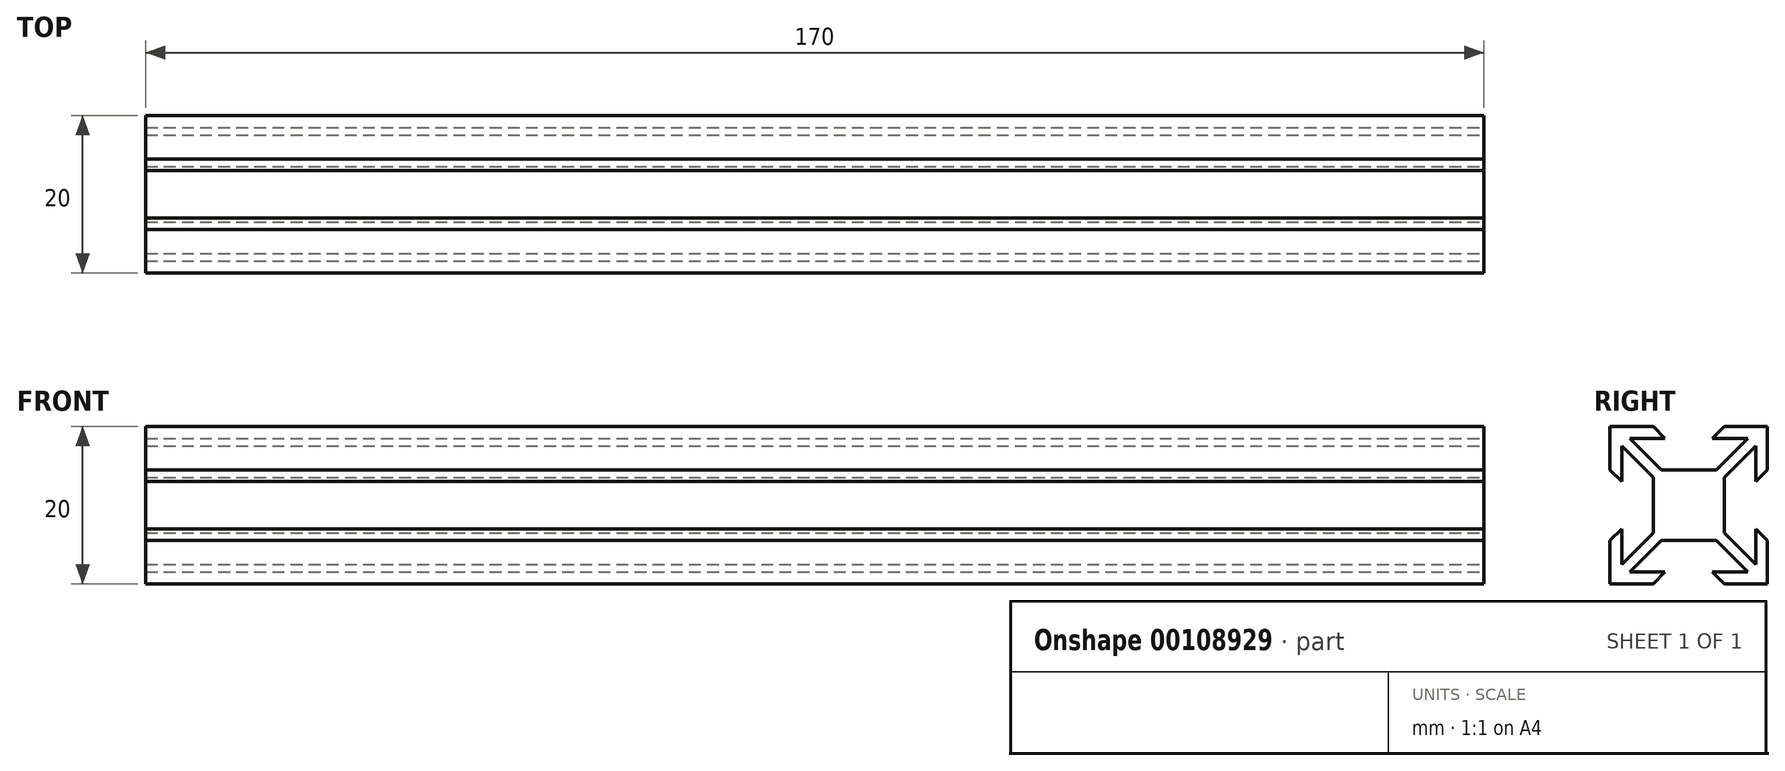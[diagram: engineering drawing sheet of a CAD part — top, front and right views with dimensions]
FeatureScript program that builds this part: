
annotation { "Feature Type Name" : "Feature", "Feature Type Description" : "" }
export const myFeature = defineFeature(function(context is Context, id is Id, definition is map)
    precondition{}
    {
        {
            var Q0;
            Q0=qCreatedBy(makeId("Top.planeOp"),FACE);
            var sketch = newSketch(context, id + "F0", { "sketchPlane" : qUnion([Q0])});
            skLineSegment(sketch, "E0.bottom", {"start": v(85, -10) * mm, "end": v(-85, -10) * mm});
            skLineSegment(sketch, "E0.top", {"start": v(85, 10) * mm, "end": v(-85, 10) * mm});
            skLineSegment(sketch, "E0.left", {"start": v(85, -10) * mm, "end": v(85, 10) * mm});
            skLineSegment(sketch, "E0.right", {"start": v(-85, -10) * mm, "end": v(-85, 10) * mm});
            skPoint(sketch, "E0.middle", {"position": v(0, 0) * mm});
            skSolve(sketch);
        }
        {
            var Q0;
            Q0 = qSketchRegion(id + "F0", true);
            extrude(context, id + "F1", {"entities" : qUnion([Q0]), "endBound" : BoundingType.SYMMETRIC, "depth" : 20 * mm});
        }
        {
            var Q0;
            Q0=makeQuery(id+"F1.opExtrude","SWEPT_FACE",FACE,{"disambiguationData":[OSD([sQuery(id+"F0.wireOp",EDGE,"E0.left")])]});
            var sketch = newSketch(context, id + "F2", { "sketchPlane" : qUnion([Q0])});
            skLineSegment(sketch, "E1", {"start": v(-4.5, 10) * mm, "end": v(-3, 8.5) * mm});
            skLineSegment(sketch, "E2", {"start": v(-3, 8.5) * mm, "end": v(-7.5, 8.5) * mm});
            skLineSegment(sketch, "E3", {"start": v(-7.5, 8.5) * mm, "end": v(-3.5, 4.5) * mm});
            skLineSegment(sketch, "E4", {"start": v(-3.5, 4.5) * mm, "end": v(0, 4.5) * mm});
            skLineSegment(sketch, "E5", {"start": v(-10, 4.5) * mm, "end": v(-8.5, 3) * mm});
            skLineSegment(sketch, "E6", {"start": v(-8.5, 3) * mm, "end": v(-8.5, 7.5) * mm});
            skLineSegment(sketch, "E7", {"start": v(-8.5, 7.5) * mm, "end": v(-4.5, 3.5) * mm});
            skLineSegment(sketch, "E8", {"start": v(-4.5, 3.5) * mm, "end": v(-4.5, 0) * mm});
            skLineSegment(sketch, "E9", {"start": v(-10, 0) * mm, "end": v(10, 0) * mm, "construction": true});
            skLineSegment(sketch, "E10", {"start": v(0, 10) * mm, "end": v(0, -10) * mm, "construction": true});
            skLineSegment(sketch, "E11.MirrorCS", {"start": v(4.5, 3.5) * mm, "end": v(4.5, 0) * mm});
            skLineSegment(sketch, "E12.MirrorCS", {"start": v(8.5, 7.5) * mm, "end": v(4.5, 3.5) * mm});
            skLineSegment(sketch, "E13.MirrorCS", {"start": v(8.5, 3) * mm, "end": v(8.5, 7.5) * mm});
            skLineSegment(sketch, "E14.MirrorCS", {"start": v(10, 4.5) * mm, "end": v(8.5, 3) * mm});
            skLineSegment(sketch, "E15.MirrorCS", {"start": v(3, 8.5) * mm, "end": v(7.5, 8.5) * mm});
            skLineSegment(sketch, "E16.MirrorCS", {"start": v(4.5, 10) * mm, "end": v(3, 8.5) * mm});
            skLineSegment(sketch, "E17.MirrorCS", {"start": v(7.5, 8.5) * mm, "end": v(3.5, 4.5) * mm});
            skLineSegment(sketch, "E18.MirrorCS", {"start": v(3.5, 4.5) * mm, "end": v(0, 4.5) * mm});
            skLineSegment(sketch, "E19.MirrorCS", {"start": v(-10, -4.5) * mm, "end": v(-8.5, -3) * mm});
            skLineSegment(sketch, "E20.MirrorCS", {"start": v(-8.5, -3) * mm, "end": v(-8.5, -7.5) * mm});
            skLineSegment(sketch, "E21.MirrorCS", {"start": v(-8.5, -7.5) * mm, "end": v(-4.5, -3.5) * mm});
            skLineSegment(sketch, "E22.MirrorCS", {"start": v(-7.5, -8.5) * mm, "end": v(-3.5, -4.5) * mm});
            skLineSegment(sketch, "E23.MirrorCS", {"start": v(-4.5, -10) * mm, "end": v(-3, -8.5) * mm});
            skLineSegment(sketch, "E24.MirrorCS", {"start": v(-4.5, -3.5) * mm, "end": v(-4.5, 0) * mm});
            skLineSegment(sketch, "E25.MirrorCS", {"start": v(-3.5, -4.5) * mm, "end": v(0, -4.5) * mm});
            skLineSegment(sketch, "E26.MirrorCS", {"start": v(-3, -8.5) * mm, "end": v(-7.5, -8.5) * mm});
            skLineSegment(sketch, "E27.MirrorCS", {"start": v(3.5, -4.5) * mm, "end": v(0, -4.5) * mm});
            skLineSegment(sketch, "E28.MirrorCS", {"start": v(7.5, -8.5) * mm, "end": v(3.5, -4.5) * mm});
            skLineSegment(sketch, "E29.MirrorCS", {"start": v(3, -8.5) * mm, "end": v(7.5, -8.5) * mm});
            skLineSegment(sketch, "E30.MirrorCS", {"start": v(4.5, -10) * mm, "end": v(3, -8.5) * mm});
            skLineSegment(sketch, "E31.MirrorCS", {"start": v(8.5, -7.5) * mm, "end": v(4.5, -3.5) * mm});
            skLineSegment(sketch, "E32.MirrorCS", {"start": v(8.5, -3) * mm, "end": v(8.5, -7.5) * mm});
            skLineSegment(sketch, "E33.MirrorCS", {"start": v(10, -4.5) * mm, "end": v(8.5, -3) * mm});
            skLineSegment(sketch, "E34.MirrorCS", {"start": v(4.5, -3.5) * mm, "end": v(4.5, 0) * mm});
            skSolve(sketch);
        }
        {
            var Q0;
            {var subQ0=sQuery(id+"F2.wireOp",EDGE,"E5");Q0=makeQuery(id+"F2.imprint","IMPRINT",FACE,{"disambiguationData":[TD([[makeQuery(id+"F2.imprint","IMPRINT",EDGE,{"derivedFrom":subQ0}),-1.0]])]});}
            var Q1;
            {var subQ0=sQuery(id+"F2.wireOp",EDGE,"E1");Q1=makeQuery(id+"F2.imprint","IMPRINT",FACE,{"disambiguationData":[TD([[makeQuery(id+"F2.imprint","IMPRINT",EDGE,{"derivedFrom":subQ0}),1.0]])]});}
            var Q2;
            Q2=makeQuery(id+"F2.imprint","IMPRINT",FACE,{"disambiguationData":[TD([[makeQuery(id+"F2.imprint","IMPRINT",EDGE,{"derivedFrom":sQuery(id+"F2.wireOp",EDGE,"E11.MirrorCS")}),1.0]])]});
            var Q3;
            Q3=makeQuery(id+"F2.imprint","IMPRINT",FACE,{"disambiguationData":[TD([[makeQuery(id+"F2.imprint","IMPRINT",EDGE,{"derivedFrom":sQuery(id+"F2.wireOp",EDGE,"E22.MirrorCS")}),-1.0]])]});
            extrude(context, id + "F3", {"entities" : qUnion([Q0, Q1, Q2, Q3]), "operationType" : NewBodyOperationType.REMOVE, "endBound" : BoundingType.THROUGH_ALL, "oppositeDirection" : true, "depth" : 25 * mm});
        }
    });
